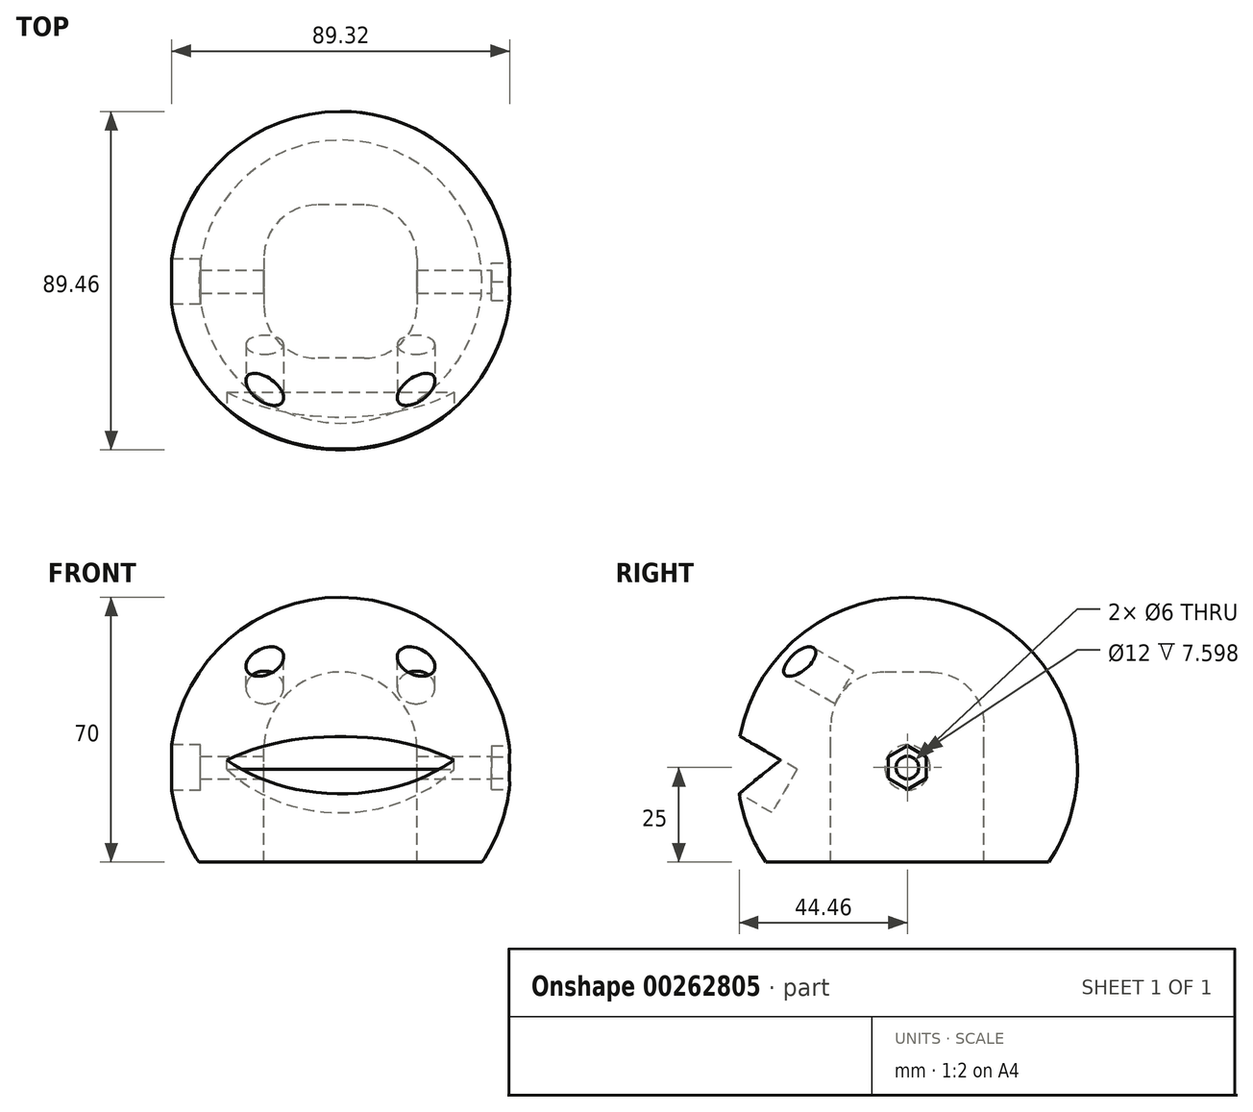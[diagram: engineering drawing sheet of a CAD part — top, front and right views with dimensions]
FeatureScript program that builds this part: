
annotation { "Feature Type Name" : "Feature", "Feature Type Description" : "" }
export const myFeature = defineFeature(function(context is Context, id is Id, definition is map)
    precondition{}
    {
        {
            var Q0;
            Q0=qCreatedBy(makeId("Top.planeOp"),FACE);
            var sketch = newSketch(context, id + "F0", { "sketchPlane" : qUnion([Q0])});
            skCircle(sketch, "E0", {"center": v(0, 0) * mm, "radius": 45 * mm});
            skLineSegment(sketch, "E1", {"start": v(0, -83.82) * mm, "end": v(0, 88.17) * mm, "construction": true});
            skLineSegment(sketch, "E2", {"start": v(0, -45) * mm, "end": v(0, 45) * mm});
            skSolve(sketch);
        }
        {
            var Q0;
            {var subQ0=sQuery(id+"F0.wireOp",EDGE,"E2");Q0=makeQuery(id+"F0.imprint","IMPRINT",FACE,{"disambiguationData":[TD([[makeQuery(id+"F0.imprint","IMPRINT",EDGE,{"derivedFrom":subQ0}),1.0]])]});}
            var Q1;
            Q1=sQuery(id+"F0.wireOp",EDGE,"E1");
            revolve(context, id + "F1", {"entities" : qUnion([Q0]), "axis" : qUnion([Q1]), "revolveType" : RevolveType.FULL});
        }
        {
            var Q0;
            Q0=qCreatedBy(makeId("Front.planeOp"),FACE);
            var sketch = newSketch(context, id + "F2", { "sketchPlane" : qUnion([Q0])});
            skLineSegment(sketch, "E3.bottom", {"start": v(-39.96, -25) * mm, "end": v(50.54, -25) * mm});
            skLineSegment(sketch, "E3.top", {"start": v(-39.96, -42.76) * mm, "end": v(50.54, -42.76) * mm});
            skLineSegment(sketch, "E3.left", {"start": v(-39.96, -25) * mm, "end": v(-39.96, -42.76) * mm});
            skLineSegment(sketch, "E3.right", {"start": v(50.54, -25) * mm, "end": v(50.54, -42.76) * mm});
            skSolve(sketch);
        }
        {
            var Q0;
            Q0 = qSketchRegion(id + "F2", true);
            extrude(context, id + "F3", {"entities" : qUnion([Q0]), "operationType" : NewBodyOperationType.REMOVE, "oppositeDirection" : true, "depth" : 80 * mm, "symmetric" : true});
        }
        {
            var Q0;
            Q0=qCreatedBy(makeId("Front.planeOp"),FACE);
            var sketch = newSketch(context, id + "F4", { "sketchPlane" : qUnion([Q0])});
            skLineSegment(sketch, "E4.bottom", {"start": v(-20.25, -54.2) * mm, "end": v(20.25, -54.2) * mm});
            skLineSegment(sketch, "E4.top", {"start": v(-20.25, 5) * mm, "end": v(20.25, 5) * mm});
            skLineSegment(sketch, "E4.left", {"start": v(-20.25, -54.2) * mm, "end": v(-20.25, 5) * mm});
            skLineSegment(sketch, "E4.right", {"start": v(20.25, -54.2) * mm, "end": v(20.25, 5) * mm});
            skCircle(sketch, "E5", {"center": v(0, 5) * mm, "radius": 20.25 * mm});
            skSolve(sketch);
        }
        {
            var Q0;
            Q0 = qSketchRegion(id + "F4", true);
            extrude(context, id + "F5", {"entities" : qUnion([Q0]), "operationType" : NewBodyOperationType.REMOVE, "oppositeDirection" : true, "depth" : 40.5 * mm, "symmetric" : true});
        }
        {
            var Q0;
            Q0=qCreatedBy(makeId("Right.planeOp"),FACE);
            var sketch = newSketch(context, id + "F6", { "sketchPlane" : qUnion([Q0])});
            skCircle(sketch, "E6", {"center": v(0, 0) * mm, "radius": 3 * mm});
            skSolve(sketch);
        }
        {
            var Q0;
            Q0 = qSketchRegion(id + "F6", true);
            extrude(context, id + "F7", {"entities" : qUnion([Q0]), "operationType" : NewBodyOperationType.REMOVE, "oppositeDirection" : true, "depth" : 100 * mm, "symmetric" : true});
        }
        {
            var Q0;
            Q0=makeQuery(id+"F5.boolean.opBoolean","COPY",EDGE,{"derivedFrom":makeQuery(id+"F5.opExtrude","CAP_EDGE",EDGE,{"disambiguationData":[OSD([sQuery(id+"F4.wireOp",EDGE,"E4.left")])],"isStart":true})});
            var Q1;
            Q1=makeQuery(id+"F5.boolean.opBoolean","COPY",EDGE,{"derivedFrom":makeQuery(id+"F5.opExtrude","CAP_EDGE",EDGE,{"disambiguationData":[OSD([sQuery(id+"F4.wireOp",EDGE,"E4.left")])],"isStart":false})});
            fillet(context, id + "F8", {"entities" : qUnion([Q0, Q1]), "radius" : 14 * mm, "tangentPropagation" : true, "allowEdgeOverflow" : false});
        }
        {
            var Q0;
            Q0=makeQuery(id+"F5.boolean.opBoolean","INTERSECT",EDGE,{"derivedFrom":[makeQuery(id+"F3.boolean.opBoolean","COPY",FACE,{"derivedFrom":makeQuery(id+"F3.opExtrude","SWEPT_FACE",FACE,{"disambiguationData":[OSD([sQuery(id+"F2.wireOp",EDGE,"E3.bottom")])]})}),makeQuery(id+"F5.opExtrude","CAP_FACE",FACE,{"disambiguationData":[OSD([sQuery(id+"F4.wireOp",EDGE,"E4.bottom"),sQuery(id+"F4.wireOp",EDGE,"E4.left"),sQuery(id+"F4.wireOp",EDGE,"E4.right"),sQuery(id+"F4.wireOp",EDGE,"E5")])],"isStart":true})]});
            cPlane(context, id + "F9", {"entities" : qUnion([Q0]), "cplaneType" : CPlaneType.LINE_ANGLE, "offset" : 25 * mm, "angle" : 30 * degree, "width" : 150 * mm, "height" : 150 * mm});
        }
        {
            var Q0;
            Q0=qCreatedBy(id+"F9.planeOp",FACE);
            cPlane(context, id + "F10", {"entities" : qUnion([Q0]), "cplaneType" : CPlaneType.OFFSET, "offset" : 60 * mm, "width" : 150 * mm, "height" : 150 * mm});
        }
        {
            var Q0;
            Q0=qCreatedBy(id+"F10.planeOp",FACE);
            var sketch = newSketch(context, id + "F11", { "sketchPlane" : qUnion([Q0])});
            skLineSegment(sketch, "E7", {"start": v(0, 0) * mm, "end": v(0, -77.27) * mm, "construction": true});
            skLineSegment(sketch, "E8", {"start": v(-30, -15) * mm, "end": v(30, -15) * mm});
            skArc(sketch, "E9", {"start": v(-30, -15) * mm, "mid": v(0, -28.24) * mm, "end": v(30, -15) * mm});
            skCircle(sketch, "E10", {"center": v(-20, 10) * mm, "radius": 5 * mm});
            skCircle(sketch, "E11.MirrorC", {"center": v(20, 10) * mm, "radius": 5 * mm});
            skSolve(sketch);
        }
        {
            var Q0;
            Q0 = qSketchRegion(id + "F11", true);
            extrude(context, id + "F12", {"entities" : qUnion([Q0]), "operationType" : NewBodyOperationType.REMOVE, "oppositeDirection" : true, "depth" : 40 * mm});
        }
        {
            var Q0;
            Q0=qCreatedBy(makeId("Right.planeOp"),FACE);
            cPlane(context, id + "F13", {"entities" : qUnion([Q0]), "cplaneType" : CPlaneType.OFFSET, "offset" : 45 * mm, "width" : 150 * mm, "height" : 150 * mm});
        }
        {
            var Q0;
            Q0=qCreatedBy(makeId("Right.planeOp"),FACE);
            cPlane(context, id + "F14", {"entities" : qUnion([Q0]), "cplaneType" : CPlaneType.OFFSET, "offset" : 45 * mm, "oppositeDirection" : true, "width" : 150 * mm, "height" : 150 * mm});
        }
        {
            var Q0;
            Q0=qCreatedBy(id+"F14.planeOp",FACE);
            var sketch = newSketch(context, id + "F15", { "sketchPlane" : qUnion([Q0])});
            skCircle(sketch, "E12", {"center": v(0, 0) * mm, "radius": 6 * mm});
            skSolve(sketch);
        }
        {
            var Q0;
            Q0 = qSketchRegion(id + "F15", true);
            extrude(context, id + "F16", {"entities" : qUnion([Q0]), "operationType" : NewBodyOperationType.REMOVE, "depth" : 8 * mm});
        }
        {
            var Q0;
            Q0=qCreatedBy(id+"F13.planeOp",FACE);
            var sketch = newSketch(context, id + "F17", { "sketchPlane" : qUnion([Q0])});
            skCircle(sketch, "E13.cCircle", {"center": v(0, 0) * mm, "radius": 5 * mm, "construction": true});
            skLineSegment(sketch, "E13.0", {"start": v(5, 2.89) * mm, "end": v(5, -2.89) * mm});
            skLineSegment(sketch, "E13.1", {"start": v(5, -2.89) * mm, "end": v(0, -5.77) * mm});
            skLineSegment(sketch, "E13.2", {"start": v(0, -5.77) * mm, "end": v(-5, -2.89) * mm});
            skLineSegment(sketch, "E13.3", {"start": v(-5, -2.89) * mm, "end": v(-5, 2.89) * mm});
            skLineSegment(sketch, "E13.4", {"start": v(-5, 2.89) * mm, "end": v(0, 5.77) * mm});
            skLineSegment(sketch, "E13.5", {"start": v(0, 5.77) * mm, "end": v(5, 2.89) * mm});
            skPoint(sketch, "E13.0.midPoint", {"position": v(5, 0) * mm});
            skSolve(sketch);
        }
        {
            var Q0;
            Q0 = qSketchRegion(id + "F17", true);
            extrude(context, id + "F18", {"entities" : qUnion([Q0]), "operationType" : NewBodyOperationType.REMOVE, "oppositeDirection" : true, "depth" : 5 * mm});
        }
    });
